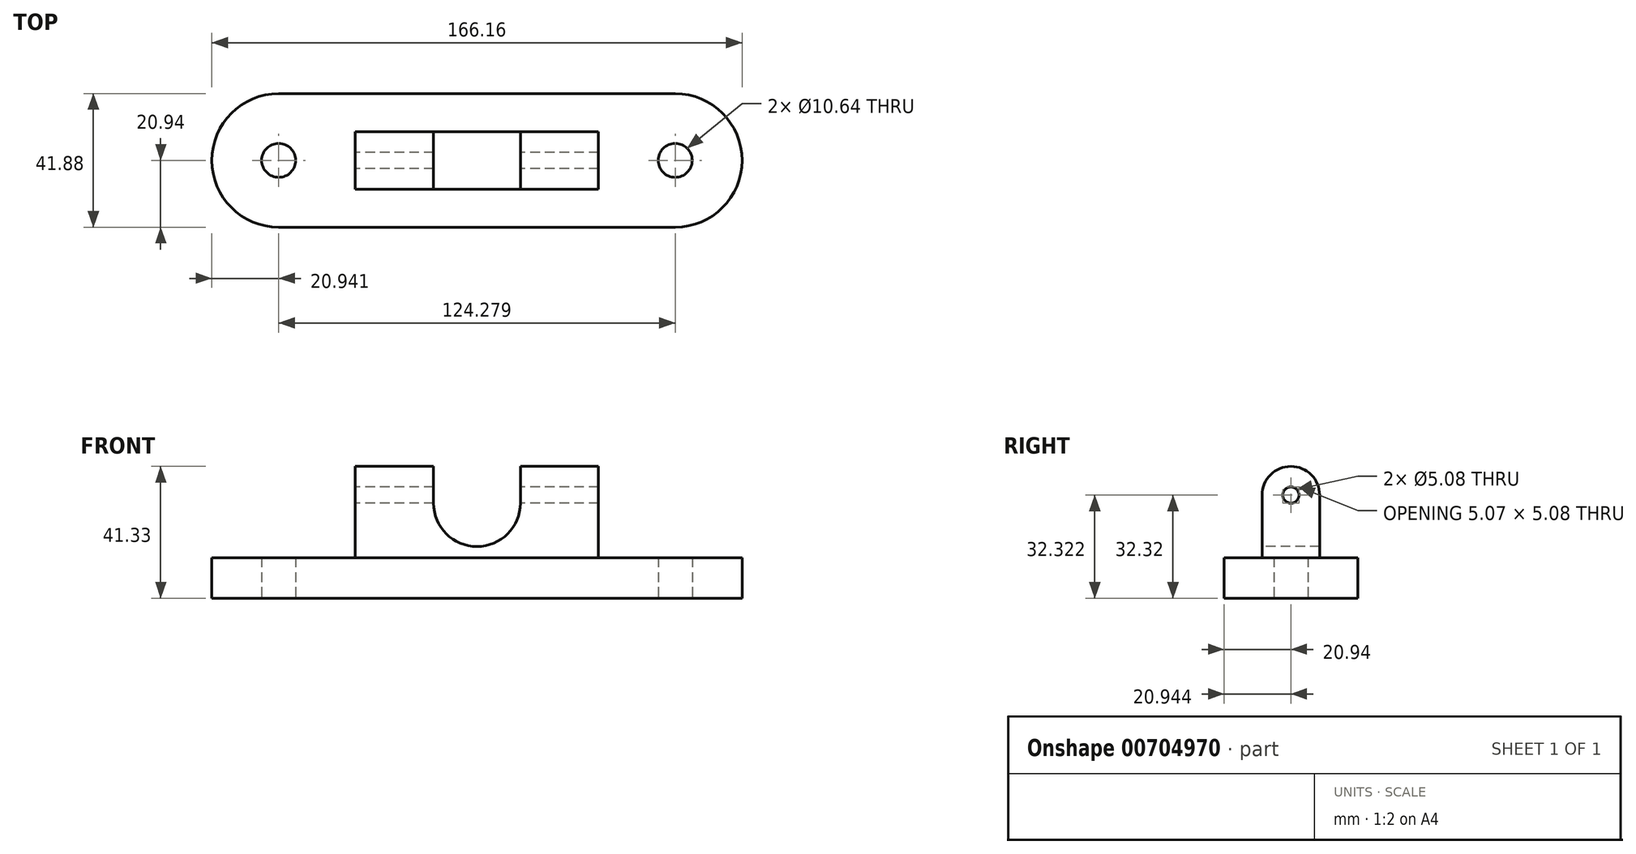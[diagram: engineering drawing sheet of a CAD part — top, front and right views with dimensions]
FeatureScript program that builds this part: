
annotation { "Feature Type Name" : "Feature", "Feature Type Description" : "" }
export const myFeature = defineFeature(function(context is Context, id is Id, definition is map)
    precondition{}
    {
        {
            var Q0;
            Q0=qCreatedBy(makeId("Top.planeOp"),FACE);
            var sketch = newSketch(context, id + "F0", { "sketchPlane" : qUnion([Q0])});
            skLineSegment(sketch, "E0", {"start": v(0, 20.94) * mm, "end": v(-62.14, 20.94) * mm});
            skArc(sketch, "E1", {"start": v(-62.14, 20.94) * mm, "mid": v(-76.95, 14.8) * mm, "end": v(-83.08, 0) * mm});
            skLineSegment(sketch, "E2.MirrorCS", {"start": v(0, -20.94) * mm, "end": v(-62.14, -20.94) * mm});
            skArc(sketch, "E3.MirrorCS", {"start": v(-62.14, -20.94) * mm, "mid": v(-76.95, -14.8) * mm, "end": v(-83.08, 0) * mm});
            skLineSegment(sketch, "E4.MirrorCS", {"start": v(0, 20.94) * mm, "end": v(62.14, 20.94) * mm});
            skArc(sketch, "E5.MirrorCS", {"start": v(62.14, 20.94) * mm, "mid": v(76.95, 14.8) * mm, "end": v(83.08, 0) * mm});
            skArc(sketch, "E6.MirrorCS", {"start": v(62.14, -20.94) * mm, "mid": v(76.95, -14.8) * mm, "end": v(83.08, 0) * mm});
            skLineSegment(sketch, "E7.MirrorCS", {"start": v(0, -20.94) * mm, "end": v(62.14, -20.94) * mm});
            skCircle(sketch, "E8", {"center": v(-62.14, 0) * mm, "radius": 5.32 * mm});
            skCircle(sketch, "E9", {"center": v(62.14, 0) * mm, "radius": 5.32 * mm});
            skSolve(sketch);
        }
        {
            var Q0;
            Q0 = qSketchRegion(id + "F0", true);
            extrude(context, id + "F1", {"entities" : qUnion([Q0]), "depth" : 12.7 * mm, "offsetDistance" : 25.4 * mm});
        }
        {
            var Q0;
            Q0=qCreatedBy(makeId("Right.planeOp"),FACE);
            var sketch = newSketch(context, id + "F2", { "sketchPlane" : qUnion([Q0])});
            skLineSegment(sketch, "E10.0", {"start": v(0, 12.7) * mm, "end": v(9, 12.7) * mm});
            skLineSegment(sketch, "E11", {"start": v(9, 12.7) * mm, "end": v(9, 32.32) * mm});
            skArc(sketch, "E12", {"start": v(9, 32.32) * mm, "mid": v(6.37, 38.7) * mm, "end": v(0, 41.33) * mm});
            skArc(sketch, "E13", {"start": v(0, 34.86) * mm, "mid": v(2.54, 32.32) * mm, "end": v(0, 29.78) * mm});
            skPoint(sketch, "E14.orphan", {"position": v(20.94, 12.7) * mm});
            skLineSegment(sketch, "E15", {"start": v(0, 12.7) * mm, "end": v(0, 41.33) * mm, "construction": true});
            skPoint(sketch, "E16.orphan", {"position": v(-20.94, 12.7) * mm});
            skArc(sketch, "E17.MirrorCS", {"start": v(-9, 32.32) * mm, "mid": v(-6.37, 38.7) * mm, "end": v(0, 41.33) * mm});
            skLineSegment(sketch, "E18.MirrorCS", {"start": v(-9, 12.7) * mm, "end": v(-9, 32.32) * mm});
            skLineSegment(sketch, "E19.MirrorCS", {"start": v(0, 12.7) * mm, "end": v(-9, 12.7) * mm});
            skArc(sketch, "E20.MirrorCS", {"start": v(0, 34.86) * mm, "mid": v(-2.54, 32.32) * mm, "end": v(0, 29.78) * mm});
            skSolve(sketch);
        }
        {
            var Q0;
            Q0 = qSketchRegion(id + "F2", true);
            extrude(context, id + "F3", {"entities" : qUnion([Q0]), "operationType" : NewBodyOperationType.ADD, "depth" : 38.1 * mm, "offsetDistance" : 25.4 * mm, "hasSecondDirection" : true, "secondDirectionOppositeDirection" : true, "secondDirectionDepth" : 38.1 * mm});
        }
        {
            var Q0;
            Q0=qCreatedBy(makeId("Front.planeOp"),FACE);
            var sketch = newSketch(context, id + "F4", { "sketchPlane" : qUnion([Q0])});
            skLineSegment(sketch, "E21", {"start": v(-13.6, 41.33) * mm, "end": v(13.6, 41.33) * mm});
            skLineSegment(sketch, "E22", {"start": v(-13.6, 41.33) * mm, "end": v(-13.6, 29.8) * mm});
            skArc(sketch, "E23", {"start": v(-13.6, 29.8) * mm, "mid": v(-9.61, 20.19) * mm, "end": v(0, 16.2) * mm});
            skLineSegment(sketch, "E24.MirrorCS", {"start": v(13.6, 41.33) * mm, "end": v(13.6, 29.8) * mm});
            skArc(sketch, "E25.MirrorCS", {"start": v(13.6, 29.8) * mm, "mid": v(9.61, 20.19) * mm, "end": v(0, 16.2) * mm});
            skSolve(sketch);
        }
        {
            var Q0;
            Q0 = qSketchRegion(id + "F4", true);
            extrude(context, id + "F5", {"entities" : qUnion([Q0]), "operationType" : NewBodyOperationType.REMOVE, "endBound" : BoundingType.THROUGH_ALL, "oppositeDirection" : true, "depth" : 25.4 * mm, "offsetDistance" : 25.4 * mm, "hasSecondDirection" : true, "secondDirectionBound" : SecondDirectionBoundingType.THROUGH_ALL, "secondDirectionOppositeDirection" : false, "secondDirectionDepth" : 25.4 * mm});
        }
    });
